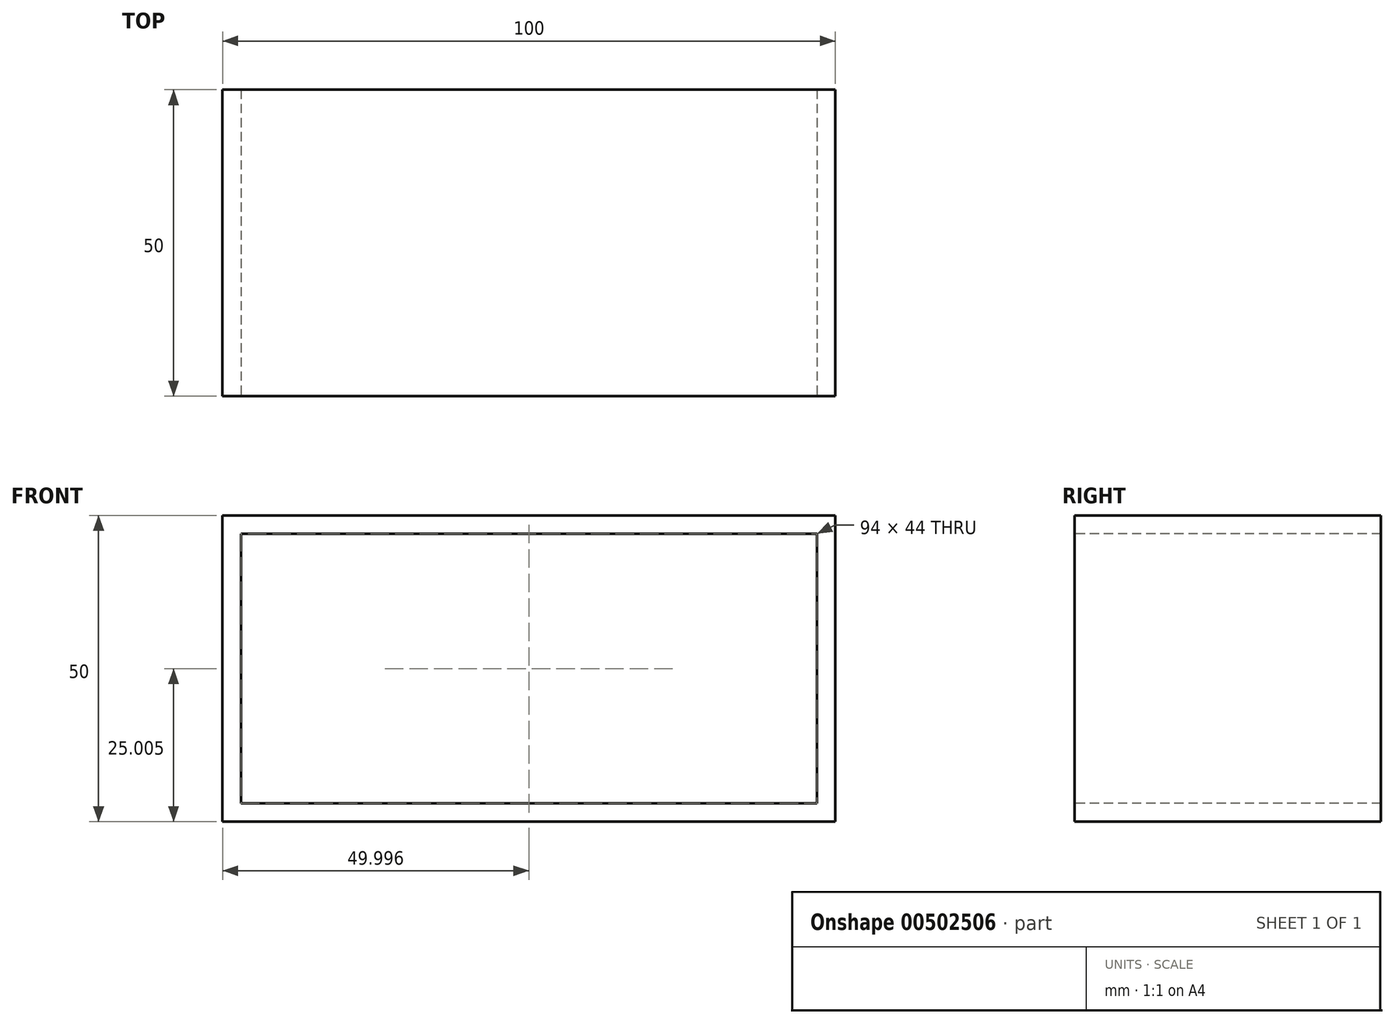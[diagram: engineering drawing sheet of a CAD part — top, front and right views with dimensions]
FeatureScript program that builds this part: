
annotation { "Feature Type Name" : "Feature", "Feature Type Description" : "" }
export const myFeature = defineFeature(function(context is Context, id is Id, definition is map)
    precondition{}
    {
        {
            var Q0;
            Q0=qCreatedBy(makeId("Front.planeOp"),FACE);
            var sketch = newSketch(context, id + "F0", { "sketchPlane" : qUnion([Q0])});
            skLineSegment(sketch, "E0.bottom", {"start": v(-50.71, 22.98) * mm, "end": v(49.29, 22.98) * mm});
            skLineSegment(sketch, "E0.top", {"start": v(-50.71, -27.02) * mm, "end": v(49.29, -27.02) * mm});
            skLineSegment(sketch, "E0.left", {"start": v(-50.71, 22.98) * mm, "end": v(-50.71, -27.02) * mm});
            skLineSegment(sketch, "E0.right", {"start": v(49.29, 22.98) * mm, "end": v(49.29, -27.02) * mm});
            skSolve(sketch);
        }
        {
            var Q0;
            Q0=makeQuery(id+"F0.imprint","IMPRINT",FACE,{"disambiguationData":[TD([[makeQuery(id+"F0.imprint","IMPRINT",EDGE,{"derivedFrom":sQuery(id+"F0.wireOp",EDGE,"E0.bottom")}),-1.0]])]});
            extrude(context, id + "F1", {"entities" : qUnion([Q0]), "depth" : 50 * mm, "offsetDistance" : 25 * mm});
        }
        {
            var Q0;
            Q0=makeQuery(id+"F1.opExtrude","CAP_FACE",FACE,{"disambiguationData":[OSD([sQuery(id+"F0.wireOp",EDGE,"E0.bottom"),sQuery(id+"F0.wireOp",EDGE,"E0.top"),sQuery(id+"F0.wireOp",EDGE,"E0.left"),sQuery(id+"F0.wireOp",EDGE,"E0.right")])],"isStart":false});
            var sketch = newSketch(context, id + "F2", { "sketchPlane" : qUnion([Q0])});
            skLineSegment(sketch, "E1.bottom", {"start": v(46.29, 19.98) * mm, "end": v(-47.71, 19.98) * mm});
            skLineSegment(sketch, "E1.top", {"start": v(46.29, -24.02) * mm, "end": v(-47.71, -24.02) * mm});
            skLineSegment(sketch, "E1.left", {"start": v(46.29, 19.98) * mm, "end": v(46.29, -24.02) * mm});
            skLineSegment(sketch, "E1.right", {"start": v(-47.71, 19.98) * mm, "end": v(-47.71, -24.02) * mm});
            skSolve(sketch);
        }
        {
            var Q0;
            Q0=makeQuery(id+"F2.imprint","IMPRINT",FACE,{"disambiguationData":[TD([[makeQuery(id+"F2.imprint","IMPRINT",EDGE,{"derivedFrom":sQuery(id+"F2.wireOp",EDGE,"E1.bottom")}),1.0]])]});
            extrude(context, id + "F3", {"entities" : qUnion([Q0]), "operationType" : NewBodyOperationType.REMOVE, "endBound" : BoundingType.UP_TO_NEXT, "oppositeDirection" : true, "depth" : 25 * mm, "offsetDistance" : 25 * mm});
        }
    });
